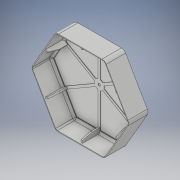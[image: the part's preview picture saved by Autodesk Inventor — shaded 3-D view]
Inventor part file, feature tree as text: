
AUTODESK INVENTOR PART (.ipt)
format: ipt  version: 2019 (Build 230136000, 136)  size: 304,128 bytes
history: native  units: mm
features: sketch x7, extrude x4, plane x3, fillet x3, other x3, projected_geometry x3, shell x1, pattern_circular x1
ambient origin geometry x8: Origin, YZ Plane, XZ Plane, XY Plane, X Axis, Y Axis, Z Axis, Center Point
bodies: Solid1 (feature_tree)
feature tree (25):
  extrude  "Extrusion1"  Depth=40.0mm TaperAngle=0.0deg
  shell  "Shell1"  Thickness=1.5mm
  plane  "Work Plane1"
  plane  "Work Plane2"
  plane  "Work Plane3"
  extrude  "Extrusion5"  Depth=10.0mm
  extrude  "Extrusion6"  Depth=5.0mm
  extrude  "Extrusion8"  TaperAngle=60.0deg  [1 undecoded]
  pattern_circular  "Circular Pattern1"  [2 undecoded]
  fillet  "Fillet1"  Radius=5.0mm
  fillet  "Fillet2"  Radius=2.0mm
  fillet  "Fillet4"  Radius=3.0mm
  sketch  "Sketch5"  dims[d12=1.0mm d37=5.0mm]
  sketch  "Sketch6"  dims[d44=10.0mm d45=60.0deg]
  sketch  "Sketch7"  dims[d46=90.0deg]
  other  "Work Axis4"
  other  "Work Axis5"
  other  "Work Axis6"
  sketch  "Sketch1"  dims[d0=175.0mm d2=40.0mm d3=0.0mm d4=1.5mm]
  sketch  "Sketch4"  dims[d10=4.0mm d11=10.0mm]
  projected_geometry  "Projected Loop3"
  sketch  "Sketch8"  dims[d47=90.0deg]
  projected_geometry  "Projected Loop4"
  sketch  "Sketch9"  dims[d52=5.5mm d53=0.75mm d54=0.0mm d55=5.0mm d56=2.0mm d57=3.0mm d58=10.0mm d59=36.0mm d60=0.0mm d70=60.0mm d72=360.0deg d74=60.0mm d75=360.0deg d77=5.0mm d78=20.0mm d79=20.0mm d80=0.0mm]
  projected_geometry  "Projected Loop5"
note: 3 required parameter values undecoded (feature->parameter linkage not recoverable at this tier; creation-order binding heuristic only, values carry confidence <= 0.55)
